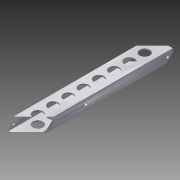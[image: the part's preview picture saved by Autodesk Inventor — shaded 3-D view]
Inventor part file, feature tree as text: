
AUTODESK INVENTOR PART (.ipt)
format: ipt  version: 2015 (Build 190159000, 159)  size: 163,328 bytes
history: native  units: in
note: dims shown in document units (in); Inventor stores cm internally (conversion verified against a paired STEP export)
features: sketch x4, hole x3, projected_geometry x3, extrude x1, pattern_linear x1
ambient origin geometry x8: Origin, YZ Plane, XZ Plane, XY Plane, X Axis, Y Axis, Z Axis, Center Point
bodies: Solid1 (feature_tree)
feature tree (12):
  extrude  "Extrusion1"  Depth=1.0in
  hole  "Hole1"  [1 undecoded]
  hole  "Hole2"  [1 undecoded]
  hole  "Hole3"  [1 undecoded]
  pattern_linear  "Rectangular Pattern1"  Spacing1=0.5in  [1 undecoded]
  sketch  "Sketch1"  dims[d0=2.0in d1=1.0in]
  sketch  "Sketch2"  dims[d2=1.75in d3=0.75in]
  projected_geometry  "Projected Loop1"
  sketch  "Sketch3"  dims[d4=0.125in d5=0.125in]
  projected_geometry  "Projected Loop2"
  sketch  "Sketch4"  dims[d6=14.25in d7=0.0in d8=0.5in d9=0.5in d10=8.5in d11=0.5in d12=0.25in d13=0.75in d14=0.375in d15=0.25in d16=0.5635in d17=1.0in d18=0.8108in d19=0.5in d20=0.5in d21=0.25in d22=0.75in d23=0.375in d24=0.25in d25=0.5635in d26=1.0in d27=0.8108in d28=1.0in d29=2.0in d30=1.0in d31=0.75in d32=0.375in d33=0.25in d34=0.5635in d35=1.0in d36=0.8108in d37=3.1496in d39=1.5in]
  projected_geometry  "Projected Loop3"
note: 4 required parameter values undecoded (feature->parameter linkage not recoverable at this tier; creation-order binding heuristic only, values carry confidence <= 0.55)
